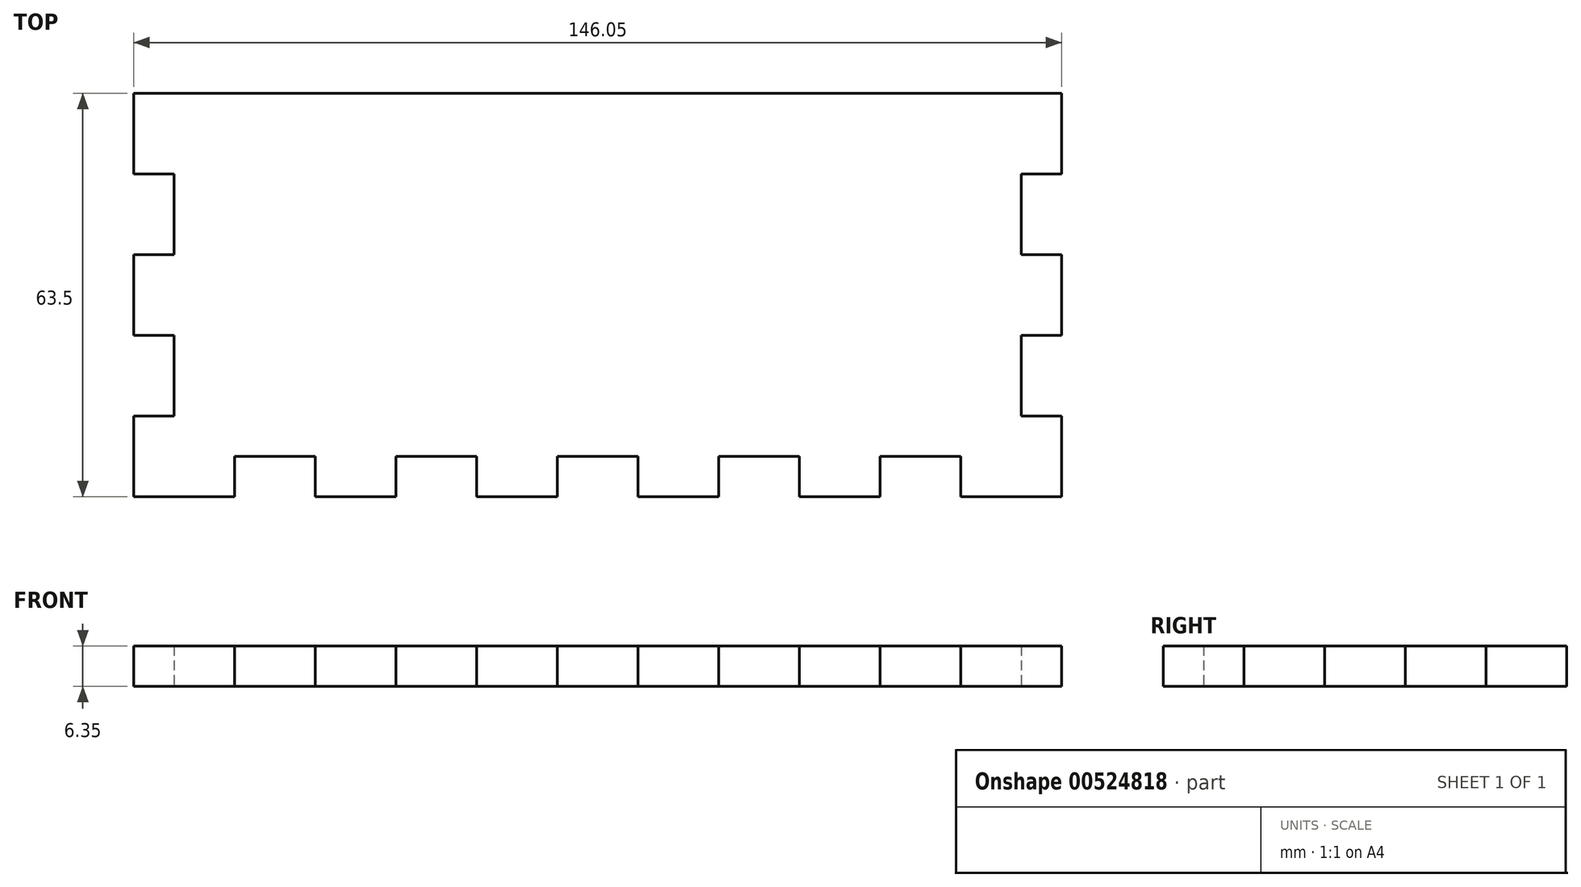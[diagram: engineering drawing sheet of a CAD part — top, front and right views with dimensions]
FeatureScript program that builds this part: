
annotation { "Feature Type Name" : "Feature", "Feature Type Description" : "" }
export const myFeature = defineFeature(function(context is Context, id is Id, definition is map)
    precondition{}
    {
        {
            var Q0;
            Q0=qCreatedBy(makeId("Top.planeOp"),FACE);
            var sketch = newSketch(context, id + "F0", { "sketchPlane" : qUnion([Q0])});
            skLineSegment(sketch, "E0.bottom", {"start": v(0, 0) * mm, "end": v(146.05, 0) * mm});
            skLineSegment(sketch, "E0.top", {"start": v(0, -63.5) * mm, "end": v(15.88, -63.5) * mm});
            skLineSegment(sketch, "E0.left", {"start": v(0, 0) * mm, "end": v(0, -12.7) * mm});
            skLineSegment(sketch, "E1", {"start": v(15.88, -63.5) * mm, "end": v(15.88, -57.15) * mm});
            skLineSegment(sketch, "E2", {"start": v(15.88, -57.15) * mm, "end": v(28.58, -57.15) * mm});
            skLineSegment(sketch, "E3", {"start": v(28.58, -57.15) * mm, "end": v(28.58, -63.5) * mm});
            skLineSegment(sketch, "E4", {"start": v(28.58, -63.5) * mm, "end": v(41.28, -63.5) * mm});
            skLineSegment(sketch, "E5", {"start": v(41.28, -63.5) * mm, "end": v(41.28, -57.15) * mm});
            skLineSegment(sketch, "E6", {"start": v(41.28, -57.15) * mm, "end": v(53.98, -57.15) * mm});
            skLineSegment(sketch, "E7", {"start": v(53.98, -57.15) * mm, "end": v(53.98, -63.5) * mm});
            skLineSegment(sketch, "E8", {"start": v(53.98, -63.5) * mm, "end": v(66.68, -63.5) * mm});
            skLineSegment(sketch, "E9", {"start": v(66.68, -63.5) * mm, "end": v(66.68, -57.15) * mm});
            skLineSegment(sketch, "E10", {"start": v(66.68, -57.15) * mm, "end": v(79.38, -57.15) * mm});
            skLineSegment(sketch, "E11", {"start": v(79.38, -57.15) * mm, "end": v(79.38, -63.5) * mm});
            skLineSegment(sketch, "E12.trimOffspring", {"start": v(28.57, -63.5) * mm, "end": v(41.28, -63.5) * mm});
            skLineSegment(sketch, "E13.trimOffspring", {"start": v(79.38, -63.5) * mm, "end": v(92.08, -63.5) * mm});
            skLineSegment(sketch, "E14", {"start": v(92.08, -63.5) * mm, "end": v(92.08, -57.15) * mm});
            skLineSegment(sketch, "E15", {"start": v(92.08, -57.15) * mm, "end": v(104.78, -57.15) * mm});
            skLineSegment(sketch, "E16", {"start": v(104.78, -57.15) * mm, "end": v(104.78, -63.5) * mm});
            skLineSegment(sketch, "E17", {"start": v(104.78, -63.5) * mm, "end": v(117.48, -63.5) * mm});
            skLineSegment(sketch, "E18", {"start": v(117.48, -63.5) * mm, "end": v(117.48, -57.15) * mm});
            skLineSegment(sketch, "E19", {"start": v(117.48, -57.15) * mm, "end": v(130.18, -57.15) * mm});
            skLineSegment(sketch, "E20", {"start": v(130.18, -57.15) * mm, "end": v(130.18, -63.5) * mm});
            skLineSegment(sketch, "E21.trimOffspring", {"start": v(130.18, -63.5) * mm, "end": v(146.05, -63.5) * mm});
            skLineSegment(sketch, "E22", {"start": v(0, -63.5) * mm, "end": v(0, -50.8) * mm});
            skLineSegment(sketch, "E23", {"start": v(0, -50.8) * mm, "end": v(6.35, -50.8) * mm});
            skLineSegment(sketch, "E24", {"start": v(6.35, -50.8) * mm, "end": v(6.35, -38.1) * mm});
            skLineSegment(sketch, "E25", {"start": v(6.35, -38.1) * mm, "end": v(0, -38.1) * mm});
            skLineSegment(sketch, "E26", {"start": v(0, -38.1) * mm, "end": v(0, -25.4) * mm});
            skLineSegment(sketch, "E27", {"start": v(0, -25.4) * mm, "end": v(6.35, -25.4) * mm});
            skLineSegment(sketch, "E28", {"start": v(6.35, -25.4) * mm, "end": v(6.35, -12.7) * mm});
            skLineSegment(sketch, "E29", {"start": v(6.35, -12.7) * mm, "end": v(0, -12.7) * mm});
            skLineSegment(sketch, "E30.trimOffspring", {"start": v(0, -25.4) * mm, "end": v(0, -38.1) * mm});
            skLineSegment(sketch, "E31.trimOffspring", {"start": v(0, -50.8) * mm, "end": v(0, -63.5) * mm});
            skLineSegment(sketch, "E32", {"start": v(73.03, -57.15) * mm, "end": v(73.03, -31.75) * mm, "construction": true});
            skLineSegment(sketch, "E33.MirrorCS", {"start": v(146.05, 0) * mm, "end": v(146.05, -12.7) * mm});
            skLineSegment(sketch, "E34.MirrorCS", {"start": v(139.7, -12.7) * mm, "end": v(146.05, -12.7) * mm});
            skLineSegment(sketch, "E35.MirrorCS", {"start": v(139.7, -25.4) * mm, "end": v(139.7, -12.7) * mm});
            skLineSegment(sketch, "E36.MirrorCS", {"start": v(146.05, -25.4) * mm, "end": v(139.7, -25.4) * mm});
            skLineSegment(sketch, "E37.MirrorCS", {"start": v(146.05, -38.1) * mm, "end": v(146.05, -25.4) * mm});
            skLineSegment(sketch, "E38.MirrorCS", {"start": v(139.7, -38.1) * mm, "end": v(146.05, -38.1) * mm});
            skLineSegment(sketch, "E39.MirrorCS", {"start": v(139.7, -50.8) * mm, "end": v(139.7, -38.1) * mm});
            skLineSegment(sketch, "E40.MirrorCS", {"start": v(146.05, -50.8) * mm, "end": v(139.7, -50.8) * mm});
            skLineSegment(sketch, "E41.MirrorCS", {"start": v(146.05, -50.8) * mm, "end": v(146.05, -63.5) * mm});
            skSolve(sketch);
        }
        {
            var Q0;
            Q0=makeQuery(id+"F0.imprint","IMPRINT",FACE,{"disambiguationData":[TD([[makeQuery(id+"F0.imprint","IMPRINT",EDGE,{"derivedFrom":sQuery(id+"F0.wireOp",EDGE,"E0.bottom")}),-1.0]])]});
            extrude(context, id + "F1", {"entities" : qUnion([Q0]), "depth" : 6.35 * mm, "offsetDistance" : 25.4 * mm});
        }
    });
